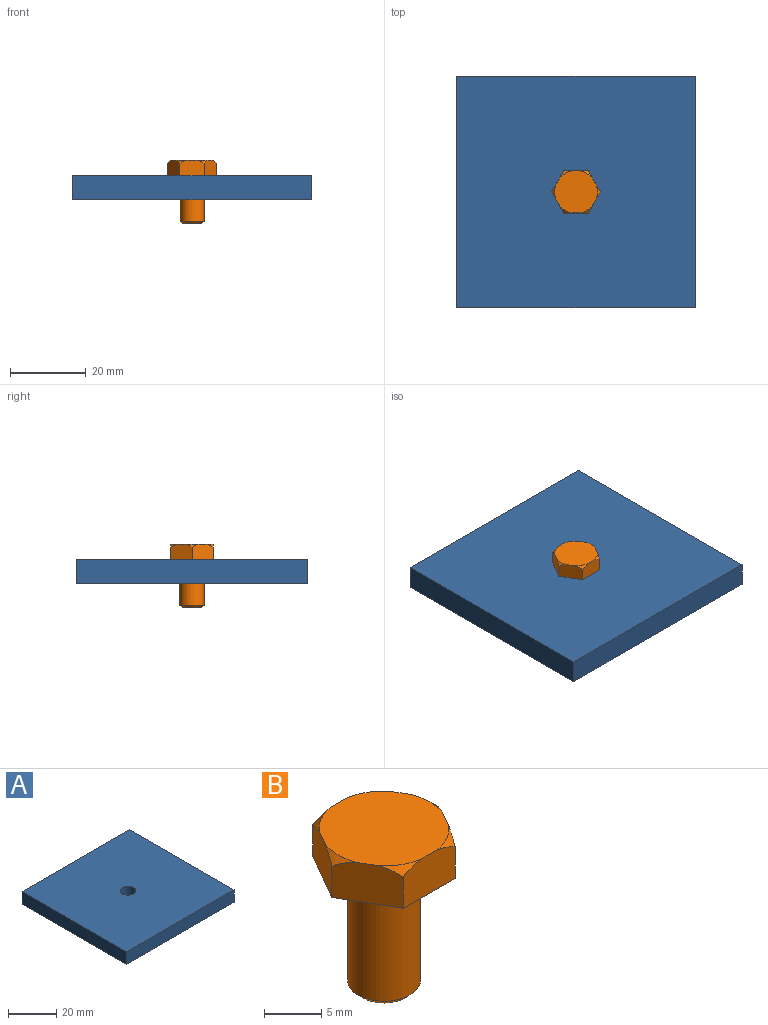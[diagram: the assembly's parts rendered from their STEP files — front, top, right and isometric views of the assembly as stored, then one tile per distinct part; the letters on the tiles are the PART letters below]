
ASSEMBLY  parts=2 mates=1
PART A: 7 faces, bbox 63x61.1x6.4 mm
  f0: plane 61.14x6.35mm, normal (1,0,0), area 388.2mm2, adj f1,f4,f5,f6
  f1: plane 62.96x6.35mm, normal (0,1,0), area 399.8mm2, adj f0,f2,f5,f6
  f2: plane 61.14x6.35mm, normal (-1,0,0), area 388.2mm2, adj f1,f4,f5,f6
  f3: cylinder r=3.17mm len=6.35mm, axis (0,0,1), area 126.7mm2, adj f5,f6
  f4: plane 62.96x6.35mm, normal (0,-1,0), area 399.8mm2, adj f0,f2,f5,f6
  f5: plane 62.96x61.14mm, normal (0,0,-1), area 3817.4mm2, adj f0,f1,f2,f3,f4
  f6: plane 62.96x61.14mm, normal (0,0,1), area 3817.4mm2, adj f0,f1,f2,f3,f4
PART B: 18 faces, bbox 12.9x12.6x16.8 mm
  f0: plane 5.08x5.08mm, normal (0,0,-1), area 20.3mm2, adj f17
  f1: cylinder r=3.17mm len=11.75mm, axis (0,0,-1), area 234.4mm2, adj f16,f17
  f2: plane 12.85x11.13mm, normal (0,0,-1), area 68.9mm2, adj f3,f4,f5,f6,f7,f8,f16
  f3: plane 5.57x4.14mm, normal (0.87,0.5,0), area 25.2mm2, adj f2,f4,f6,f9,f13,f15
  f4: plane 6.43x4.14mm, normal (0,1,0), area 25.2mm2, adj f2,f3,f5,f9,f14,f15
  f5: plane 5.57x4.14mm, normal (-0.87,0.5,0), area 25.2mm2, adj f2,f4,f7,f9,f12,f14
  f6: plane 5.57x4.14mm, normal (0.87,-0.5,0), area 25.2mm2, adj f2,f3,f8,f9,f11,f13
  f7: plane 5.57x4.14mm, normal (-0.87,-0.5,0), area 25.2mm2, adj f2,f5,f8,f9,f10,f12
  f8: plane 6.43x4.14mm, normal (0,-1,0), area 25.2mm2, adj f2,f6,f7,f9,f10,f11
  f9: plane 11.32x11.13mm, normal (0,0,1), area 99.9mm2, adj f3,f4,f5,f6,f7,f8,f10,f11
  f10: cone r=5.66mm half-angle=45deg, axis (0,0,-1), area 1.7mm2, adj f7,f8,f9
  f11: cone r=5.66mm half-angle=45deg, axis (0,0,-1), area 1.7mm2, adj f6,f8,f9
  f12: cone r=5.66mm half-angle=45deg, axis (0,0,-1), area 1.7mm2, adj f5,f7,f9
  f13: cone r=5.66mm half-angle=45deg, axis (0,0,-1), area 1.7mm2, adj f3,f6,f9
  f14: cone r=5.66mm half-angle=45deg, axis (0,0,-1), area 1.7mm2, adj f4,f5,f9
  f15: cone r=5.66mm half-angle=45deg, axis (0,0,-1), area 1.7mm2, adj f3,f4,f9
  f16: torus R=3.49mm, axis (0,0,1), area 10.3mm2, adj f1,f2
  f17: cone r=2.54mm half-angle=45deg, axis (0,0,1), area 16.1mm2, adj f0,f1
PLACE A at identity fixed
PLACE B t=(0,0,-25.4)mm
MATE fastened B.f1 <-> A.f3  axis (0,0,-1) through (0,0,0)mm
